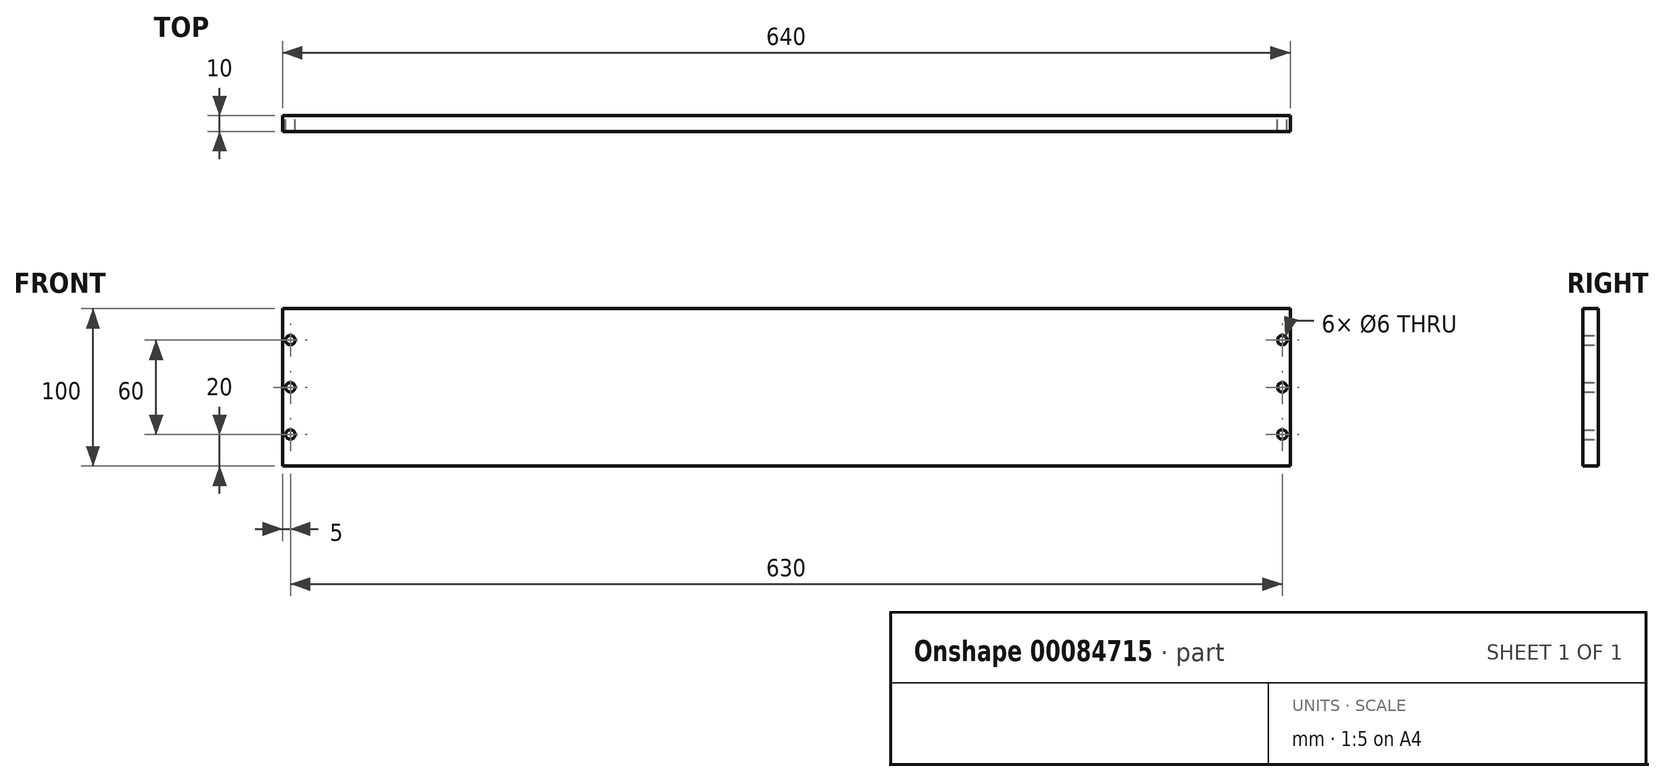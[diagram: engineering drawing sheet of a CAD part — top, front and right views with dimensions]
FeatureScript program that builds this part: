
annotation { "Feature Type Name" : "Feature", "Feature Type Description" : "" }
export const myFeature = defineFeature(function(context is Context, id is Id, definition is map)
    precondition{}
    {
        {
            var Q0;
            Q0=qCreatedBy(makeId("Front.planeOp"),FACE);
            var sketch = newSketch(context, id + "F0", { "sketchPlane" : qUnion([Q0])});
            skLineSegment(sketch, "E0.bottom", {"start": v(-320, 50) * mm, "end": v(320, 50) * mm});
            skLineSegment(sketch, "E0.top", {"start": v(-320, -50) * mm, "end": v(320, -50) * mm});
            skLineSegment(sketch, "E0.left", {"start": v(-320, 50) * mm, "end": v(-320, -50) * mm});
            skLineSegment(sketch, "E0.right", {"start": v(320, 50) * mm, "end": v(320, -50) * mm});
            skPoint(sketch, "E0.middle", {"position": v(0, 0) * mm});
            skCircle(sketch, "E1", {"center": v(-315, 30) * mm, "radius": 3 * mm});
            skCircle(sketch, "E2", {"center": v(-315, -30) * mm, "radius": 3 * mm});
            skCircle(sketch, "E3", {"center": v(315, 30) * mm, "radius": 3 * mm});
            skCircle(sketch, "E4", {"center": v(315, -30) * mm, "radius": 3 * mm});
            skCircle(sketch, "E5", {"center": v(-315, 0) * mm, "radius": 3 * mm});
            skCircle(sketch, "E6", {"center": v(315, 0) * mm, "radius": 3 * mm});
            skSolve(sketch);
        }
        {
            var Q0;
            Q0=makeQuery(id+"F0.imprint","IMPRINT",FACE,{"disambiguationData":[TD([[makeQuery(id+"F0.imprint","IMPRINT",EDGE,{"derivedFrom":sQuery(id+"F0.wireOp",EDGE,"E0.bottom")}),-1.0]])]});
            extrude(context, id + "F1", {"entities" : qUnion([Q0]), "depth" : 10 * mm});
        }
    });
